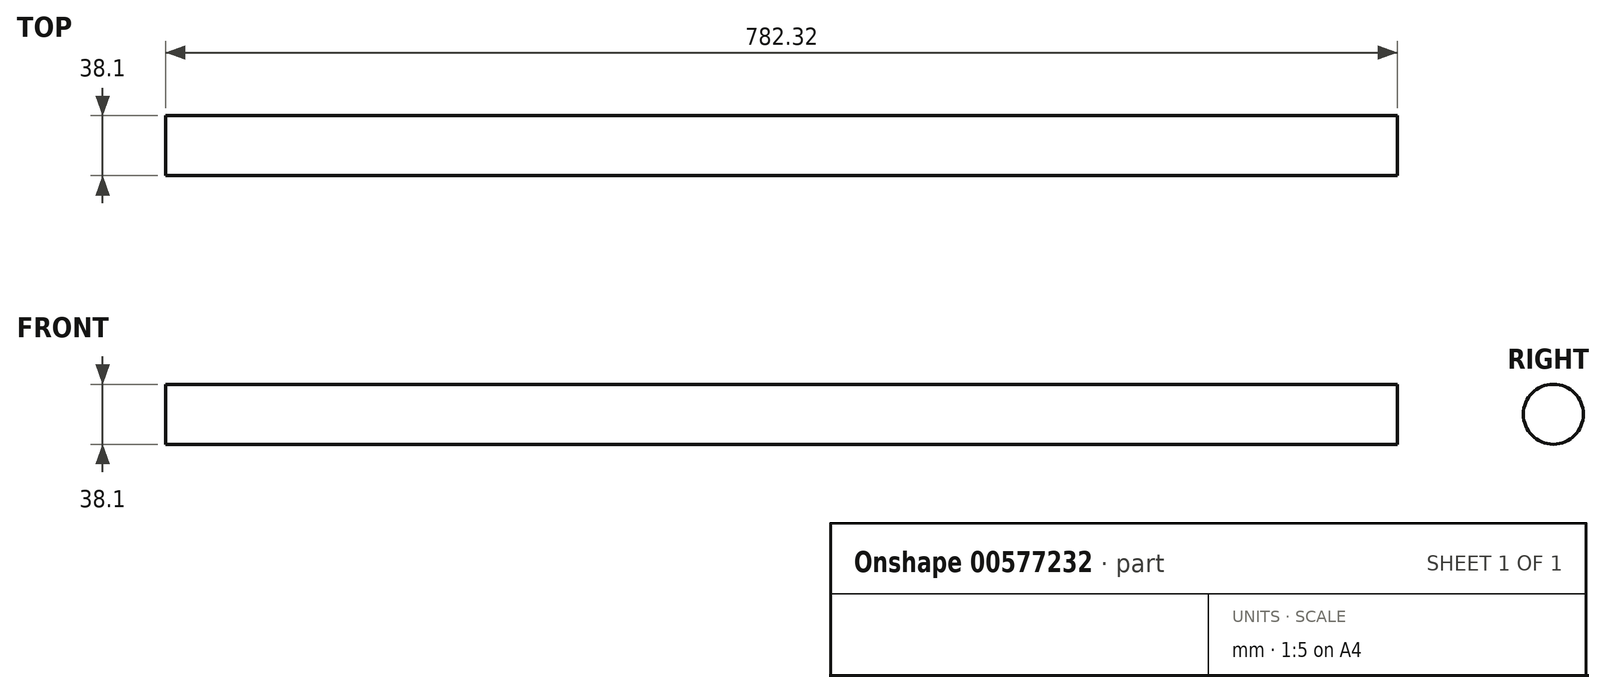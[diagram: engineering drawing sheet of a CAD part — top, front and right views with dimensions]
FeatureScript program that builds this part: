
annotation { "Feature Type Name" : "Feature", "Feature Type Description" : "" }
export const myFeature = defineFeature(function(context is Context, id is Id, definition is map)
    precondition{}
    {
        {
            var Q0;
            Q0=qCreatedBy(makeId("Right.planeOp"),FACE);
            var sketch = newSketch(context, id + "F0", { "sketchPlane" : qUnion([Q0])});
            skCircle(sketch, "E0", {"center": v(0, 0) * mm, "radius": 19.05 * mm});
            skSolve(sketch);
        }
        {
            var Q0;
            Q0=makeQuery(id+"F0.imprint","IMPRINT",FACE,{"disambiguationData":[TD([[makeQuery(id+"F0.imprint","IMPRINT",EDGE,{"derivedFrom":sQuery(id+"F0.wireOp",EDGE,"E0")}),1.0]])]});
            extrude(context, id + "F1", {"entities" : qUnion([Q0]), "depth" : 782.32 * mm, "offsetDistance" : 25.4 * mm});
        }
    });
